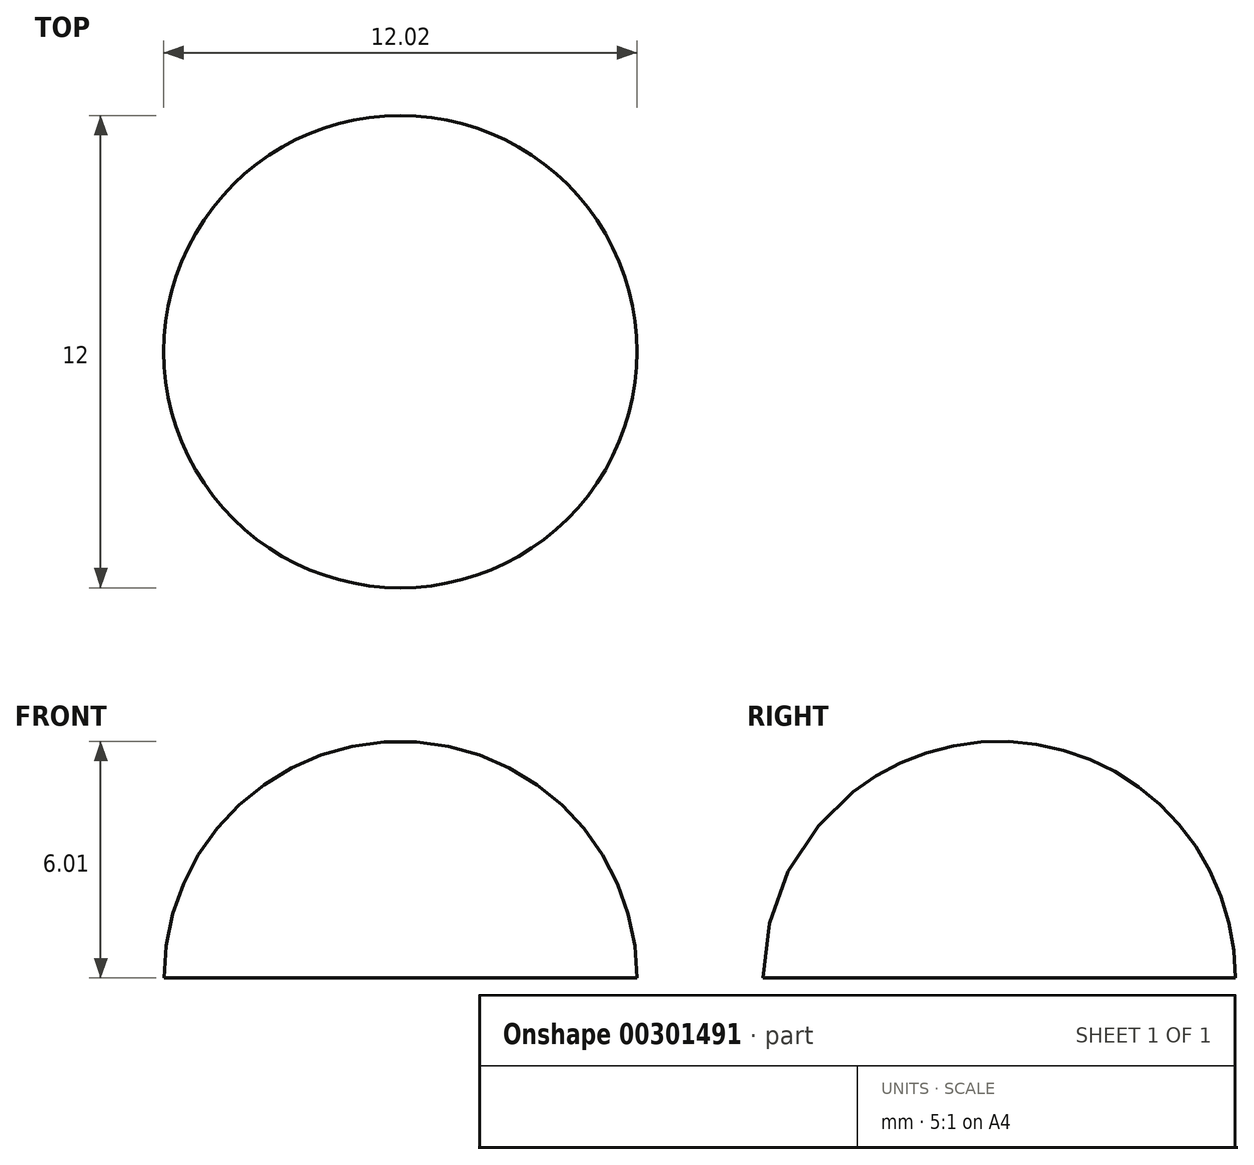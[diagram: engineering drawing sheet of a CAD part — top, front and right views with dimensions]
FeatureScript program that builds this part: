
annotation { "Feature Type Name" : "Feature", "Feature Type Description" : "" }
export const myFeature = defineFeature(function(context is Context, id is Id, definition is map)
    precondition{}
    {
        {
            var Q0;
            Q0=qCreatedBy(makeId("Top.planeOp"),FACE);
            var sketch = newSketch(context, id + "F0", { "sketchPlane" : qUnion([Q0])});
            skArc(sketch, "E0", {"start": v(13.63, 25.54) * mm, "mid": v(7.62, 19.54) * mm, "end": v(13.63, 13.54) * mm});
            skLineSegment(sketch, "E1", {"start": v(13.63, 25.54) * mm, "end": v(13.63, 13.54) * mm});
            skSolve(sketch);
        }
        {
            var Q0;
            Q0=makeQuery(id+"F0.imprint","IMPRINT",FACE,{"disambiguationData":[TD([[makeQuery(id+"F0.imprint","IMPRINT",EDGE,{"derivedFrom":sQuery(id+"F0.wireOp",EDGE,"E0")}),1.0]])]});
            var Q1;
            Q1=sQuery(id+"F0.wireOp",EDGE,"E1");
            revolve(context, id + "F1", {"entities" : qUnion([Q0]), "axis" : qUnion([Q1]), "revolveType" : RevolveType.ONE_DIRECTION, "oppositeDirection" : true, "angle" : 180 * degree});
        }
    });
